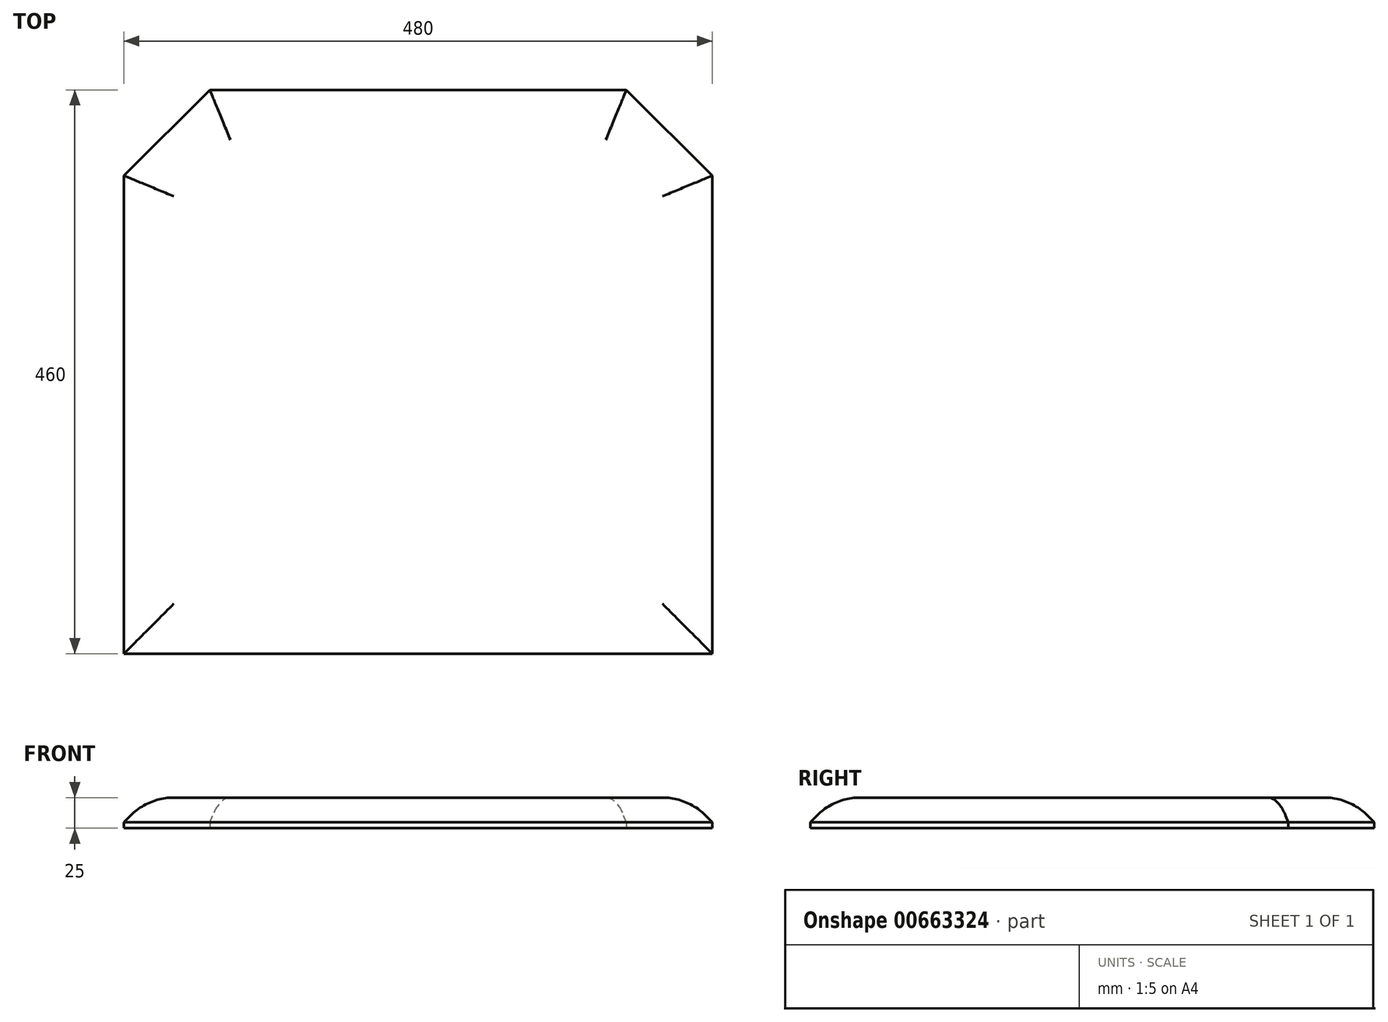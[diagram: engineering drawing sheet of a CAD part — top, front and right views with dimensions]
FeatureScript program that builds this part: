
annotation { "Feature Type Name" : "Feature", "Feature Type Description" : "" }
export const myFeature = defineFeature(function(context is Context, id is Id, definition is map)
    precondition{}
    {
        {
            var Q0;
            Q0=qCreatedBy(makeId("Top.planeOp"),FACE);
            var sketch = newSketch(context, id + "F0", { "sketchPlane" : qUnion([Q0])});
            skLineSegment(sketch, "E0.bottom", {"start": v(240, -230) * mm, "end": v(-240, -230) * mm});
            skLineSegment(sketch, "E0.top", {"start": v(170, 230) * mm, "end": v(-170, 230) * mm});
            skLineSegment(sketch, "E0.left", {"start": v(240, -230) * mm, "end": v(240, 160) * mm});
            skLineSegment(sketch, "E0.right", {"start": v(-240, -230) * mm, "end": v(-240, 160) * mm});
            skPoint(sketch, "E0.middle", {"position": v(0, 0) * mm});
            skLineSegment(sketch, "E1", {"start": v(-240, 160) * mm, "end": v(-170, 230) * mm});
            skLineSegment(sketch, "E2", {"start": v(0, 230) * mm, "end": v(0, -230) * mm, "construction": true});
            skLineSegment(sketch, "E3.MirrorCS", {"start": v(240, 160) * mm, "end": v(170, 230) * mm});
            skSolve(sketch);
        }
        {
            var Q0;
            Q0=makeQuery(id+"F0.imprint","IMPRINT",FACE,{"disambiguationData":[TD([[makeQuery(id+"F0.imprint","IMPRINT",EDGE,{"derivedFrom":sQuery(id+"F0.wireOp",EDGE,"E0.bottom")}),-1.0]])]});
            extrude(context, id + "F1", {"entities" : qUnion([Q0]), "depth" : 25 * mm, "offsetDistance" : 25 * mm});
        }
        {
            var Q0;
            Q0=makeQuery(id+"F1.opExtrude","CAP_EDGE",EDGE,{"disambiguationData":[OSD([sQuery(id+"F0.wireOp",EDGE,"E3.MirrorCS")])],"isStart":false});
            var Q1;
            Q1=makeQuery(id+"F1.opExtrude","CAP_EDGE",EDGE,{"disambiguationData":[OSD([sQuery(id+"F0.wireOp",EDGE,"E1")])],"isStart":false});
            var Q2;
            Q2=makeQuery(id+"F1.opExtrude","CAP_EDGE",EDGE,{"disambiguationData":[OSD([sQuery(id+"F0.wireOp",EDGE,"E0.top")])],"isStart":false});
            var Q3;
            Q3=makeQuery(id+"F1.opExtrude","CAP_EDGE",EDGE,{"disambiguationData":[OSD([sQuery(id+"F0.wireOp",EDGE,"E0.left")])],"isStart":false});
            var Q4;
            Q4=makeQuery(id+"F1.opExtrude","CAP_EDGE",EDGE,{"disambiguationData":[OSD([sQuery(id+"F0.wireOp",EDGE,"E0.right")])],"isStart":false});
            var Q5;
            Q5=makeQuery(id+"F1.opExtrude","CAP_EDGE",EDGE,{"disambiguationData":[OSD([sQuery(id+"F0.wireOp",EDGE,"E0.bottom")])],"isStart":false});
            chamfer(context, id + "F2", {"entities" : qUnion([Q0, Q1, Q2, Q3, Q4, Q5]), "width" : 20 * mm, "tangentPropagation" : true});
        }
        {
            var Q0;
            {var subQ0=sQuery(id+"F0.wireOp",EDGE,"E0.top");Q0=makeQuery(id+"F2.opChamfer","BLEND_EDGE",EDGE,{"blendedFrom":[makeQuery(id+"F1.opExtrude","CAP_EDGE",EDGE,{"disambiguationData":[OSD([subQ0])],"isStart":false}),makeQuery(id+"F1.opExtrude","CAP_FACE",FACE,{"disambiguationData":[OSD([sQuery(id+"F0.wireOp",EDGE,"E0.bottom"),subQ0,sQuery(id+"F0.wireOp",EDGE,"E0.left"),sQuery(id+"F0.wireOp",EDGE,"E0.right"),sQuery(id+"F0.wireOp",EDGE,"E1"),sQuery(id+"F0.wireOp",EDGE,"E3.MirrorCS")])],"isStart":false})],"blendedInto":[makeQuery(id+"F1.opExtrude","CAP_FACE",FACE,{"disambiguationData":[OSD([sQuery(id+"F0.wireOp",EDGE,"E0.bottom"),subQ0,sQuery(id+"F0.wireOp",EDGE,"E0.left"),sQuery(id+"F0.wireOp",EDGE,"E0.right"),sQuery(id+"F0.wireOp",EDGE,"E1"),sQuery(id+"F0.wireOp",EDGE,"E3.MirrorCS")])],"isStart":false})]});}
            var Q1;
            {var subQ0=sQuery(id+"F0.wireOp",EDGE,"E3.MirrorCS");Q1=makeQuery(id+"F2.opChamfer","BLEND_EDGE",EDGE,{"blendedFrom":[makeQuery(id+"F1.opExtrude","CAP_EDGE",EDGE,{"disambiguationData":[OSD([subQ0])],"isStart":false}),makeQuery(id+"F1.opExtrude","CAP_FACE",FACE,{"disambiguationData":[OSD([sQuery(id+"F0.wireOp",EDGE,"E0.bottom"),sQuery(id+"F0.wireOp",EDGE,"E0.top"),sQuery(id+"F0.wireOp",EDGE,"E0.left"),sQuery(id+"F0.wireOp",EDGE,"E0.right"),sQuery(id+"F0.wireOp",EDGE,"E1"),subQ0])],"isStart":false})],"blendedInto":[makeQuery(id+"F1.opExtrude","CAP_FACE",FACE,{"disambiguationData":[OSD([sQuery(id+"F0.wireOp",EDGE,"E0.bottom"),sQuery(id+"F0.wireOp",EDGE,"E0.top"),sQuery(id+"F0.wireOp",EDGE,"E0.left"),sQuery(id+"F0.wireOp",EDGE,"E0.right"),sQuery(id+"F0.wireOp",EDGE,"E1"),subQ0])],"isStart":false})]});}
            var Q2;
            {var subQ0=sQuery(id+"F0.wireOp",EDGE,"E0.left");Q2=makeQuery(id+"F2.opChamfer","BLEND_EDGE",EDGE,{"blendedFrom":[makeQuery(id+"F1.opExtrude","CAP_EDGE",EDGE,{"disambiguationData":[OSD([subQ0])],"isStart":false}),makeQuery(id+"F1.opExtrude","CAP_FACE",FACE,{"disambiguationData":[OSD([sQuery(id+"F0.wireOp",EDGE,"E0.bottom"),sQuery(id+"F0.wireOp",EDGE,"E0.top"),subQ0,sQuery(id+"F0.wireOp",EDGE,"E0.right"),sQuery(id+"F0.wireOp",EDGE,"E1"),sQuery(id+"F0.wireOp",EDGE,"E3.MirrorCS")])],"isStart":false})],"blendedInto":[makeQuery(id+"F1.opExtrude","CAP_FACE",FACE,{"disambiguationData":[OSD([sQuery(id+"F0.wireOp",EDGE,"E0.bottom"),sQuery(id+"F0.wireOp",EDGE,"E0.top"),subQ0,sQuery(id+"F0.wireOp",EDGE,"E0.right"),sQuery(id+"F0.wireOp",EDGE,"E1"),sQuery(id+"F0.wireOp",EDGE,"E3.MirrorCS")])],"isStart":false})]});}
            var Q3;
            {var subQ0=sQuery(id+"F0.wireOp",EDGE,"E1");Q3=makeQuery(id+"F2.opChamfer","BLEND_EDGE",EDGE,{"blendedFrom":[makeQuery(id+"F1.opExtrude","CAP_EDGE",EDGE,{"disambiguationData":[OSD([subQ0])],"isStart":false}),makeQuery(id+"F1.opExtrude","CAP_FACE",FACE,{"disambiguationData":[OSD([sQuery(id+"F0.wireOp",EDGE,"E0.bottom"),sQuery(id+"F0.wireOp",EDGE,"E0.top"),sQuery(id+"F0.wireOp",EDGE,"E0.left"),sQuery(id+"F0.wireOp",EDGE,"E0.right"),subQ0,sQuery(id+"F0.wireOp",EDGE,"E3.MirrorCS")])],"isStart":false})],"blendedInto":[makeQuery(id+"F1.opExtrude","CAP_FACE",FACE,{"disambiguationData":[OSD([sQuery(id+"F0.wireOp",EDGE,"E0.bottom"),sQuery(id+"F0.wireOp",EDGE,"E0.top"),sQuery(id+"F0.wireOp",EDGE,"E0.left"),sQuery(id+"F0.wireOp",EDGE,"E0.right"),subQ0,sQuery(id+"F0.wireOp",EDGE,"E3.MirrorCS")])],"isStart":false})]});}
            var Q4;
            {var subQ0=sQuery(id+"F0.wireOp",EDGE,"E0.right");Q4=makeQuery(id+"F2.opChamfer","BLEND_EDGE",EDGE,{"blendedFrom":[makeQuery(id+"F1.opExtrude","CAP_EDGE",EDGE,{"disambiguationData":[OSD([subQ0])],"isStart":false}),makeQuery(id+"F1.opExtrude","CAP_FACE",FACE,{"disambiguationData":[OSD([sQuery(id+"F0.wireOp",EDGE,"E0.bottom"),sQuery(id+"F0.wireOp",EDGE,"E0.top"),sQuery(id+"F0.wireOp",EDGE,"E0.left"),subQ0,sQuery(id+"F0.wireOp",EDGE,"E1"),sQuery(id+"F0.wireOp",EDGE,"E3.MirrorCS")])],"isStart":false})],"blendedInto":[makeQuery(id+"F1.opExtrude","CAP_FACE",FACE,{"disambiguationData":[OSD([sQuery(id+"F0.wireOp",EDGE,"E0.bottom"),sQuery(id+"F0.wireOp",EDGE,"E0.top"),sQuery(id+"F0.wireOp",EDGE,"E0.left"),subQ0,sQuery(id+"F0.wireOp",EDGE,"E1"),sQuery(id+"F0.wireOp",EDGE,"E3.MirrorCS")])],"isStart":false})]});}
            var Q5;
            {var subQ0=sQuery(id+"F0.wireOp",EDGE,"E0.bottom");Q5=makeQuery(id+"F2.opChamfer","BLEND_EDGE",EDGE,{"blendedFrom":[makeQuery(id+"F1.opExtrude","CAP_EDGE",EDGE,{"disambiguationData":[OSD([subQ0])],"isStart":false}),makeQuery(id+"F1.opExtrude","CAP_FACE",FACE,{"disambiguationData":[OSD([subQ0,sQuery(id+"F0.wireOp",EDGE,"E0.top"),sQuery(id+"F0.wireOp",EDGE,"E0.left"),sQuery(id+"F0.wireOp",EDGE,"E0.right"),sQuery(id+"F0.wireOp",EDGE,"E1"),sQuery(id+"F0.wireOp",EDGE,"E3.MirrorCS")])],"isStart":false})],"blendedInto":[makeQuery(id+"F1.opExtrude","CAP_FACE",FACE,{"disambiguationData":[OSD([subQ0,sQuery(id+"F0.wireOp",EDGE,"E0.top"),sQuery(id+"F0.wireOp",EDGE,"E0.left"),sQuery(id+"F0.wireOp",EDGE,"E0.right"),sQuery(id+"F0.wireOp",EDGE,"E1"),sQuery(id+"F0.wireOp",EDGE,"E3.MirrorCS")])],"isStart":false})]});}
            fillet(context, id + "F3", {"entities" : qUnion([Q0, Q1, Q2, Q3, Q4, Q5]), "radius" : 50 * mm, "tangentPropagation" : true, "allowEdgeOverflow" : false});
        }
    });
